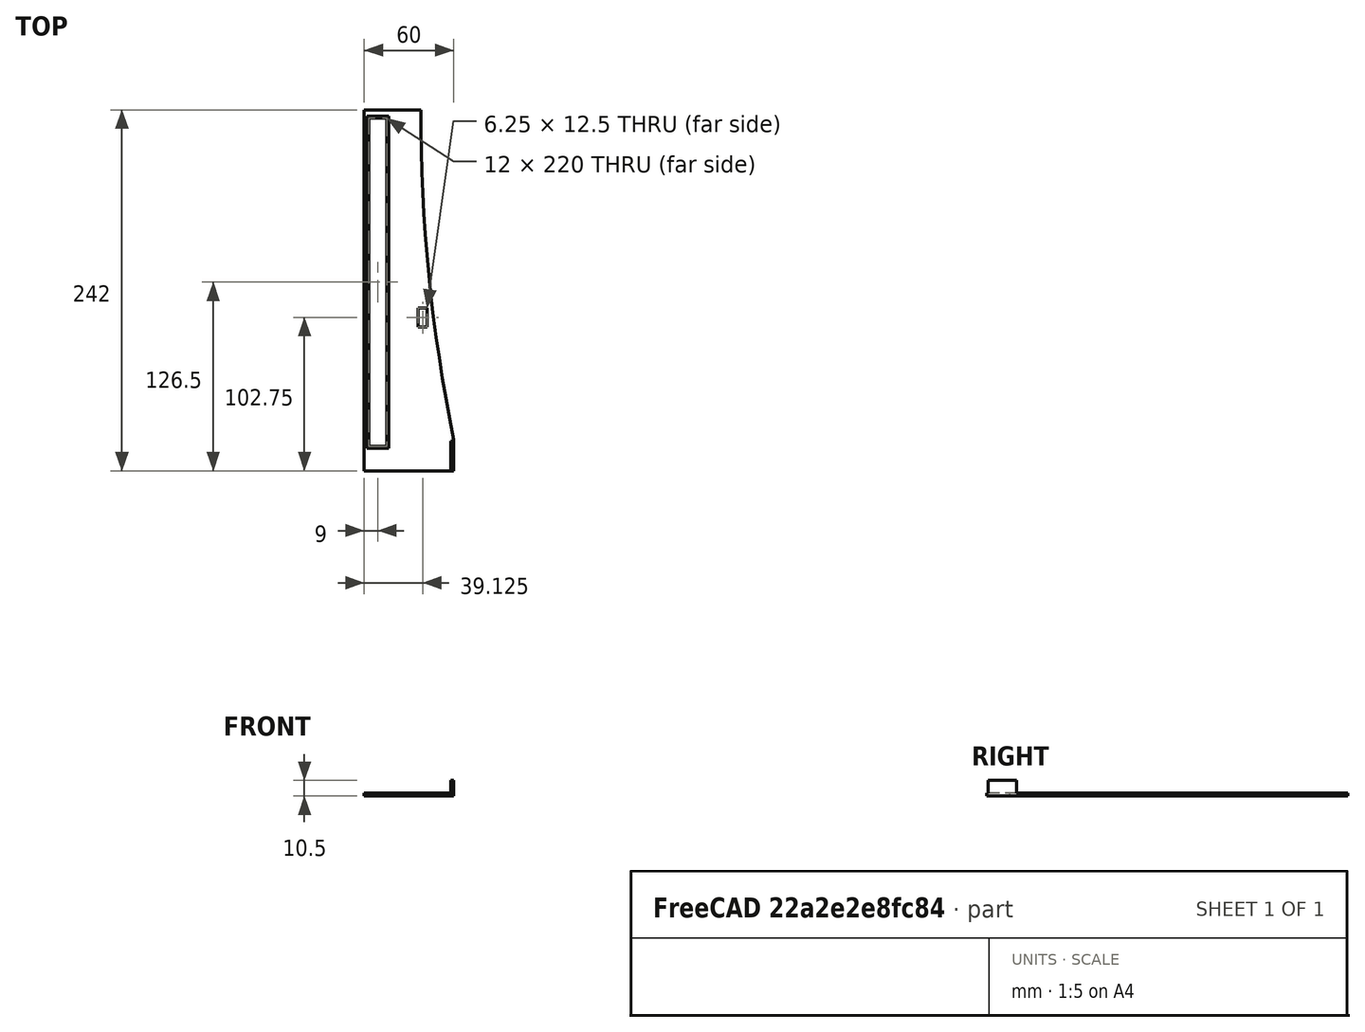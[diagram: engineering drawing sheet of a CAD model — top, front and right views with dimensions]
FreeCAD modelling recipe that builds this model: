
FCSTD DOCUMENT  (FreeCAD 0.19R)
Label: case-top
License: All rights reserved
LicenseURL: http://en.wikipedia.org/wiki/All_rights_reserved
objects: Sketcher::SketchObject×5, PartDesign::Pocket×3, PartDesign::Pad×2, Image::ImagePlane×1, PartDesign::Body×1, Mesh::Feature×1
note: 16 computed .brp shape members not serialized (recipe doc carries the construction recipe); baked Part::Feature solids carry a one-line shape summary decoded from their .brp

FEATURE [Image::ImagePlane] ImagePlane
  Placement = pos=(37,121,0) rot=(0,-1,0;3.14159rad)
  XSize = 74
  YSize = 240
FEATURE [Sketcher::SketchObject] Sketch
  FullyConstrained = true
  MapMode = 5
  Support = -> [XY_Plane]
  sketch-geometry (5):
    g0: LineSegment StartX=7 StartY=0 StartZ=0 EndX=67 EndY=0 EndZ=0
    g1: LineSegment StartX=45 StartY=242 StartZ=0 EndX=7 EndY=242 EndZ=0
    g2: LineSegment StartX=7 StartY=0 StartZ=0 EndX=7 EndY=242 EndZ=0
    g3: LineSegment StartX=67 StartY=0 StartZ=0 EndX=67 EndY=21 EndZ=0
    g4: ArcOfCircle CenterX=1119.99 CenterY=237.418 CenterZ=0 NormalX=0 NormalY=0 NormalZ=1 AngleXU=0 Radius=1075 StartAngle=3.13733 EndAngle=3.3443
  constraints (16):
    c: PointOnObject(g0,g-1)
    c: PointOnObject(g0,g-1)
    c: Horizontal(g1)
    c: Coincident(g2,g0)
    c: Coincident(g2,g1)
    c: Vertical(g2)
    c: Coincident(g3,g0)
    c: Vertical(g3)
    c: Coincident(g4,g1)
    c: Coincident(g4,g3)
    c: DistanceX(g-1,g0) = 7
    c: DistanceX(g0,g0) = 60
    c: DistanceY(g2,g2) = 242
    c: DistanceY(g3,g3) = 21
    c: DistanceX(g1,g1) = 38
    c: Diameter(g4) = 2150
FEATURE [PartDesign::Pad] Pad
  Direction = (1,1,1)
  Length = 2
  Length2 = 100
  Profile = -> Sketch
  Type = 0
FEATURE [Sketcher::SketchObject] Sketch001
  FullyConstrained = true
  MapMode = 5
  Placement = pos=(0,0,2) rot=(0,0,1;0rad)
  Support = -> [Pad]
  sketch-geometry (4):
    g0: LineSegment StartX=65 StartY=1 StartZ=0 EndX=67 EndY=1 EndZ=0
    g1: LineSegment StartX=67 StartY=1 StartZ=0 EndX=67 EndY=20 EndZ=0
    g2: LineSegment StartX=67 StartY=20 StartZ=0 EndX=65 EndY=20 EndZ=0
    g3: LineSegment StartX=65 StartY=20 StartZ=0 EndX=65 EndY=1 EndZ=0
  constraints (12):
    c: Coincident(g0,g1)
    c: Coincident(g1,g2)
    c: Coincident(g2,g3)
    c: Coincident(g3,g0)
    c: Horizontal(g0)
    c: Horizontal(g2)
    c: Vertical(g1)
    c: Vertical(g3)
    c: DistanceX(g2,g2) = 2
    c: DistanceY(g1,g1) = 19
    c: DistanceY(g-1,g0) = 1
    c: DistanceX(g-1,g0) = 65
FEATURE [PartDesign::Pad] Pad001
  BaseFeature = -> Pad
  Direction = (1,1,1)
  Length = 8.5
  Length2 = 100
  Profile = -> Sketch001
  Type = 0
FEATURE [Sketcher::SketchObject] Sketch002
  FullyConstrained = true
  MapMode = 5
  Placement = pos=(0,0,2) rot=(0,0,1;0rad)
  Support = -> [Pad001]
  sketch-geometry (4):
    g0: LineSegment StartX=10 StartY=16.5 StartZ=0 EndX=22 EndY=16.5 EndZ=0
    g1: LineSegment StartX=22 StartY=16.5 StartZ=0 EndX=22 EndY=236.5 EndZ=0
    g2: LineSegment StartX=22 StartY=236.5 StartZ=0 EndX=10 EndY=236.5 EndZ=0
    g3: LineSegment StartX=10 StartY=236.5 StartZ=0 EndX=10 EndY=16.5 EndZ=0
  constraints (12):
    c: Coincident(g0,g1)
    c: Coincident(g1,g2)
    c: Coincident(g2,g3)
    c: Coincident(g3,g0)
    c: Horizontal(g0)
    c: Horizontal(g2)
    c: Vertical(g1)
    c: Vertical(g3)
    c: DistanceX(g2,g2) = 12
    c: DistanceY(g1,g1) = 220
    c: DistanceX(g-1,g0) = 10
    c: DistanceY(g-1,g0) = 16.5
FEATURE [PartDesign::Pocket] Pocket
  BaseFeature = -> Pad001
  Length = 5
  Length2 = 100
  Profile = -> Sketch002
  Type = 2
FEATURE [Sketcher::SketchObject] Sketch003
  FullyConstrained = true
  MapMode = 5
  Placement = pos=(0,0,2) rot=(0,0,1;0rad)
  Support = -> [Pocket]
  sketch-geometry (4):
    g0: LineSegment StartX=8.75 StartY=15.25 StartZ=0 EndX=23.25 EndY=15.25 EndZ=0
    g1: LineSegment StartX=23.25 StartY=15.25 StartZ=0 EndX=23.25 EndY=237.75 EndZ=0
    g2: LineSegment StartX=23.25 StartY=237.75 StartZ=0 EndX=8.75 EndY=237.75 EndZ=0
    g3: LineSegment StartX=8.75 StartY=237.75 StartZ=0 EndX=8.75 EndY=15.25 EndZ=0
  constraints (12):
    c: Coincident(g0,g1)
    c: Coincident(g1,g2)
    c: Coincident(g2,g3)
    c: Coincident(g3,g0)
    c: Horizontal(g0)
    c: Horizontal(g2)
    c: Vertical(g1)
    c: Vertical(g3)
    c: DistanceX(g2,g2) = 14.5
    c: DistanceY(g1,g1) = 222.5
    c: DistanceX(g-1,g0) = 8.75
    c: DistanceY(g-1,g0) = 15.25
FEATURE [PartDesign::Pocket] Pocket001
  BaseFeature = -> Pocket
  Length = 1.45
  Length2 = 100
  Profile = -> Sketch003
  Type = 0
FEATURE [Sketcher::SketchObject] Sketch004
  FullyConstrained = true
  MapMode = 5
  Placement = pos=(0,0,2) rot=(0,0,1;0rad)
  Support = -> [Pocket001]
  sketch-geometry (4):
    g0: LineSegment StartX=43 StartY=96.5 StartZ=0 EndX=49.25 EndY=96.5 EndZ=0
    g1: LineSegment StartX=49.25 StartY=96.5 StartZ=0 EndX=49.25 EndY=109 EndZ=0
    g2: LineSegment StartX=49.25 StartY=109 StartZ=0 EndX=43 EndY=109 EndZ=0
    g3: LineSegment StartX=43 StartY=109 StartZ=0 EndX=43 EndY=96.5 EndZ=0
  constraints (12):
    c: Coincident(g0,g1)
    c: Coincident(g1,g2)
    c: Coincident(g2,g3)
    c: Coincident(g3,g0)
    c: Horizontal(g0)
    c: Horizontal(g2)
    c: Vertical(g1)
    c: Vertical(g3)
    c: DistanceX(g2,g2) = 6.25
    c: DistanceY(g1,g1) = 12.5
    c: DistanceX(g-1,g0) = 43
    c: DistanceY(g-1,g0) = 96.5
FEATURE [PartDesign::Pocket] Pocket002
  BaseFeature = -> Pocket001
  Length = 5
  Length2 = 100
  Profile = -> Sketch004
  Type = 1
FEATURE [PartDesign::Body] Body
  Group = -> [Sketch,Pad,Sketch001,Pad001,Sketch002,Pocket,Sketch003,Pocket001,Sketch004,Pocket002]
  Origin = -> Origin
  Tip = -> Pocket002
FEATURE [Mesh::Feature] Mesh  label="Body (Meshed)"
